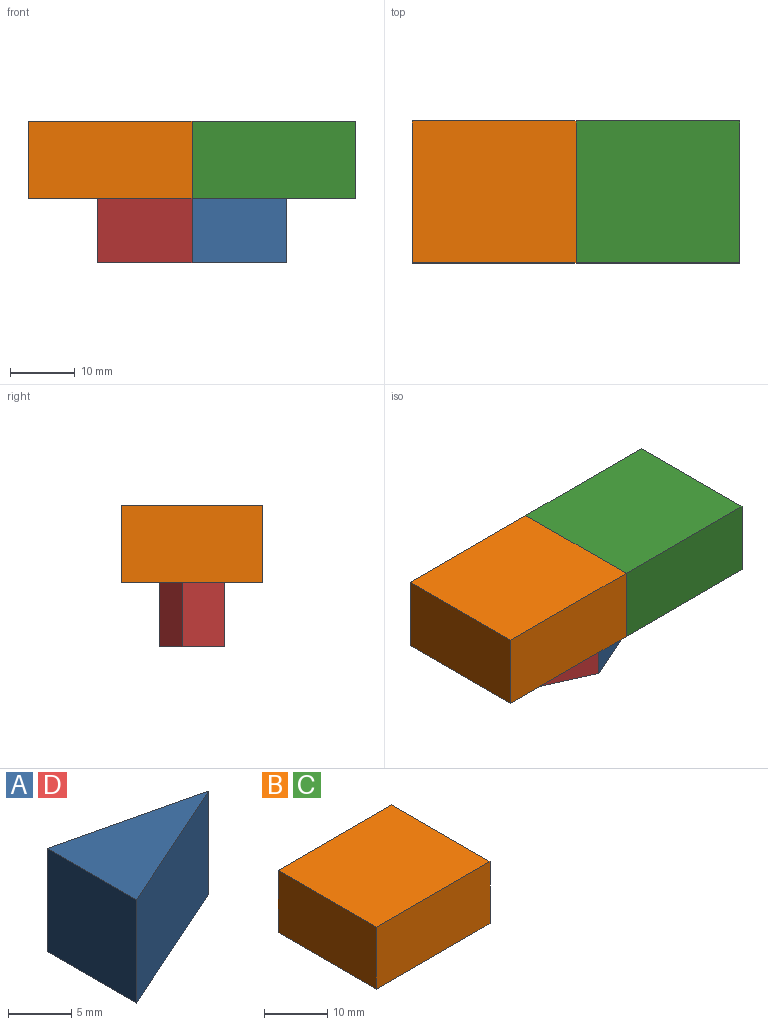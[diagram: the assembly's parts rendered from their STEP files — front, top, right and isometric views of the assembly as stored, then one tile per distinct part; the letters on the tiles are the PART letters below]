
ASSEMBLY  parts=4 mates=3
PART A: 5 faces, bbox 14.6x10x10 mm
  f0: plane 14.6x10mm, normal (0.41,-0.91,0), area 160mm2, adj f1,f2,f3,f4
  f1: plane 10x10mm, normal (-1,0,0), area 100mm2, adj f0,f2,f3,f4
  f2: plane 14.6x10mm, normal (0.23,0.97,0), area 150mm2, adj f0,f1,f3,f4
  f3: plane 14.6x10mm, normal (0,0,-1), area 73mm2, adj f0,f1,f2
  f4: plane 14.6x10mm, normal (0,0,1), area 73mm2, adj f0,f1,f2
PART B: 6 faces, bbox 25.4x22x12 mm
  f0: plane 25.4x12mm, normal (0,-1,0), area 304.8mm2, adj f1,f3,f4,f5
  f1: plane 25.4x22mm, normal (0,0,-1), area 558.8mm2, adj f0,f2,f4,f5
  f2: plane 25.4x12mm, normal (0,1,0), area 304.8mm2, adj f1,f3,f4,f5
  f3: plane 25.4x22mm, normal (0,0,1), area 558.8mm2, adj f0,f2,f4,f5
  f4: plane 22x12mm, normal (1,0,0), area 264mm2, adj f0,f1,f2,f3
  f5: plane 22x12mm, normal (-1,0,0), area 264mm2, adj f0,f1,f2,f3
PART C: same geometry as B
PART D: same geometry as A
PLACE A t=(0,6,0)mm
PLACE B rot(axis=(0,0,1),180deg) t=(0,22,0)mm
PLACE C at identity fixed
PLACE D rot(axis=(0,1,0),180deg) t=(0,6,-10)mm
MATE fastened A.f4 <-> C.f1  axis (0,0,1) through (0,11,0)mm
MATE fastened D.f1 <-> A.f1  axis (1,0,0) through (0,11,-5)mm
MATE fastened B.f5 <-> C.f5  axis (1,0,0) through (0,11,6)mm
